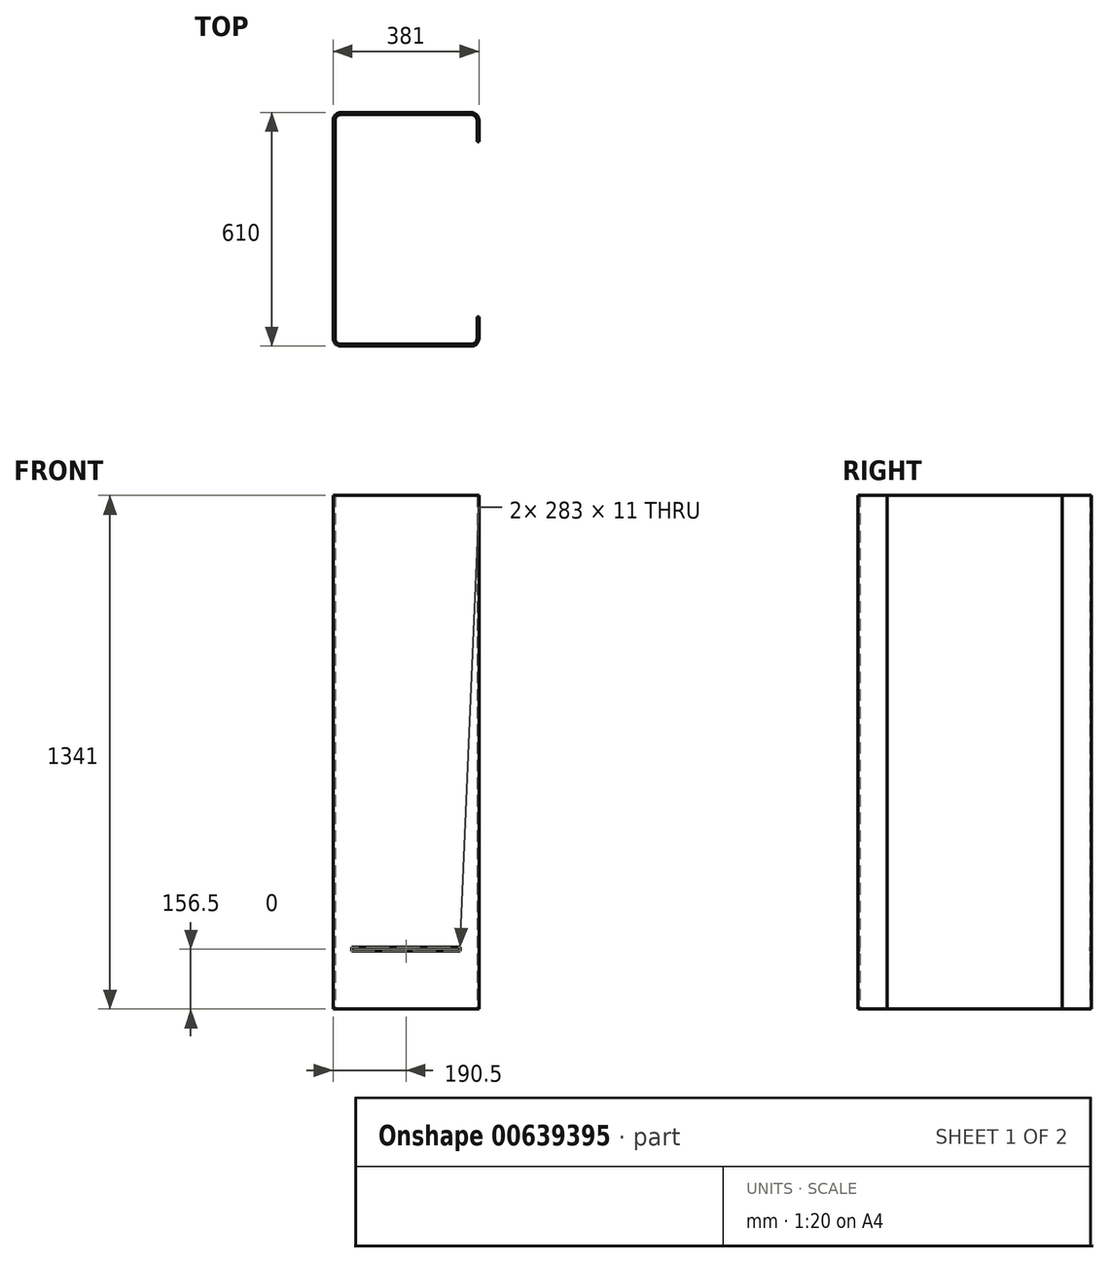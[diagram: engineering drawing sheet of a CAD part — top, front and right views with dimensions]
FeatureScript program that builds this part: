
annotation { "Feature Type Name" : "Feature", "Feature Type Description" : "" }
export const myFeature = defineFeature(function(context is Context, id is Id, definition is map)
    precondition{}
    {
        {
            var Q0;
            Q0=qCreatedBy(makeId("Top.planeOp"),FACE);
            var sketch = newSketch(context, id + "F0", { "sketchPlane" : qUnion([Q0])});
            skLineSegment(sketch, "E0.bottom", {"start": v(-21, 0) * mm, "end": v(-360, 0) * mm});
            skLineSegment(sketch, "E0.top", {"start": v(-21, 610) * mm, "end": v(-360, 610) * mm});
            skLineSegment(sketch, "E0.left", {"start": v(0, 21) * mm, "end": v(0, 76.5) * mm});
            skLineSegment(sketch, "E0.right", {"start": v(-381, 21) * mm, "end": v(-381, 589) * mm});
            skPoint(sketch, "E1.visualSharp", {"position": v(-381, 0) * mm});
            skArc(sketch, "E1.filletArc", {"start": v(-381, 21) * mm, "mid": v(-374.85, 6.15) * mm, "end": v(-360, 0) * mm});
            skPoint(sketch, "E2.visualSharp", {"position": v(-381, 610) * mm});
            skArc(sketch, "E2.filletArc", {"start": v(-360, 610) * mm, "mid": v(-374.85, 603.85) * mm, "end": v(-381, 589) * mm});
            skPoint(sketch, "E3.visualSharp", {"position": v(0, 610) * mm});
            skArc(sketch, "E3.filletArc", {"start": v(0, 589) * mm, "mid": v(-6.15, 603.85) * mm, "end": v(-21, 610) * mm});
            skPoint(sketch, "E4.visualSharp", {"position": v(0, 0) * mm});
            skArc(sketch, "E4.filletArc", {"start": v(-21, 0) * mm, "mid": v(-6.15, 6.15) * mm, "end": v(0, 21) * mm});
            skArc(sketch, "E5.0", {"start": v(-376, 21) * mm, "mid": v(-371.31, 9.69) * mm, "end": v(-360, 5) * mm});
            skLineSegment(sketch, "E6.0", {"start": v(-376, 21) * mm, "end": v(-376, 589) * mm});
            skArc(sketch, "E7.0", {"start": v(-360, 605) * mm, "mid": v(-371.31, 600.31) * mm, "end": v(-376, 589) * mm});
            skLineSegment(sketch, "E8.0", {"start": v(-21, 605) * mm, "end": v(-360, 605) * mm});
            skArc(sketch, "E9.0", {"start": v(-5, 589) * mm, "mid": v(-9.69, 600.31) * mm, "end": v(-21, 605) * mm});
            skLineSegment(sketch, "E10.0", {"start": v(-5, 21) * mm, "end": v(-5, 76.5) * mm});
            skArc(sketch, "E11.0", {"start": v(-21, 5) * mm, "mid": v(-9.69, 9.69) * mm, "end": v(-5, 21) * mm});
            skLineSegment(sketch, "E12.0", {"start": v(-21, 5) * mm, "end": v(-360, 5) * mm});
            skPoint(sketch, "E13.endSnap0", {"position": v(-5, 305) * mm});
            skLineSegment(sketch, "E14", {"start": v(-5, 76.5) * mm, "end": v(0, 76.5) * mm});
            skLineSegment(sketch, "E15", {"start": v(-5, 533.5) * mm, "end": v(0, 533.5) * mm});
            skLineSegment(sketch, "E16.trimOffspring", {"start": v(0, 533.5) * mm, "end": v(0, 589) * mm});
            skLineSegment(sketch, "E17.trimOffspring", {"start": v(-5, 533.5) * mm, "end": v(-5, 589) * mm});
            skSolve(sketch);
        }
        {
            var Q0;
            Q0 = qSketchRegion(id + "F0", true);
            extrude(context, id + "F1", {"entities" : qUnion([Q0]), "depth" : 1341 * mm, "offsetDistance" : 25 * mm});
        }
        {
            var Q0;
            Q0=makeQuery(id+"F1.opExtrude","SWEPT_FACE",FACE,{"disambiguationData":[OSD([sQuery(id+"F0.wireOp",EDGE,"E0.top")])]});
            var sketch = newSketch(context, id + "F2", { "sketchPlane" : qUnion([Q0])});
            skLineSegment(sketch, "E18.0", {"start": v(49, 162) * mm, "end": v(332, 162) * mm});
            skLineSegment(sketch, "E19.1", {"start": v(16, 1226) * mm, "end": v(16, -5) * mm});
            skLineSegment(sketch, "E19.2", {"start": v(365, 1226) * mm, "end": v(16, 1226) * mm, "construction": true});
            skLineSegment(sketch, "E19.3", {"start": v(365, -5) * mm, "end": v(365, 1226) * mm, "construction": true});
            skLineSegment(sketch, "E20.0", {"start": v(49, 151) * mm, "end": v(332, 151) * mm});
            skLineSegment(sketch, "E21.0", {"start": v(16, -5) * mm, "end": v(365, -5) * mm, "construction": true});
            skLineSegment(sketch, "E21.1", {"start": v(16, 1346) * mm, "end": v(16, -5) * mm, "construction": true});
            skLineSegment(sketch, "E21.2", {"start": v(365, 1346) * mm, "end": v(16, 1346) * mm});
            skLineSegment(sketch, "E21.3", {"start": v(365, -5) * mm, "end": v(365, 1346) * mm});
            skLineSegment(sketch, "E22", {"start": v(49, 162) * mm, "end": v(49, 151) * mm});
            skLineSegment(sketch, "E23", {"start": v(332, 162) * mm, "end": v(332, 151) * mm});
            skPoint(sketch, "E24.orphan", {"position": v(360, 162) * mm});
            skPoint(sketch, "E25.orphan", {"position": v(21, 162) * mm});
            skSolve(sketch);
        }
        {
            var Q0;
            Q0=makeQuery(id+"F2.imprint","IMPRINT",FACE,{"disambiguationData":[TD([[makeQuery(id+"F2.imprint","IMPRINT",EDGE,{"derivedFrom":sQuery(id+"F2.wireOp",EDGE,"E18.0")}),-1.0]])]});
            var Q1;
            Q1=makeQuery(id+"F1.opExtrude","SWEPT_FACE",FACE,{"disambiguationData":[OSD([sQuery(id+"F0.wireOp",EDGE,"E0.bottom")])]});
            extrude(context, id + "F3", {"entities" : qUnion([Q0]), "operationType" : NewBodyOperationType.REMOVE, "endBound" : BoundingType.UP_TO_SURFACE, "oppositeDirection" : true, "depth" : 25 * mm, "endBoundEntityFace" : qUnion([Q1]), "offsetDistance" : 25 * mm});
        }
    });
